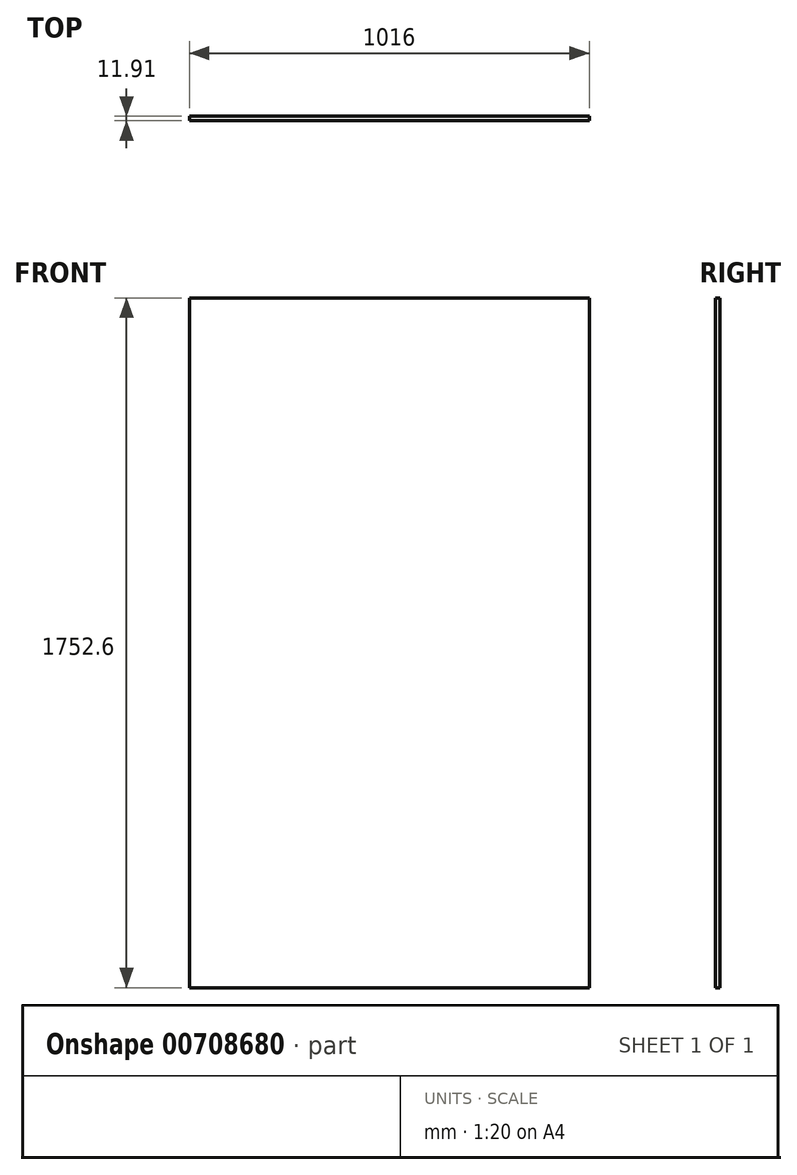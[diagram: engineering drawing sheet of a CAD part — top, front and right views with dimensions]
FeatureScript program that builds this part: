
annotation { "Feature Type Name" : "Feature", "Feature Type Description" : "" }
export const myFeature = defineFeature(function(context is Context, id is Id, definition is map)
    precondition{}
    {
        {
            var Q0;
            Q0=qCreatedBy(makeId("Front.planeOp"),FACE);
            var sketch = newSketch(context, id + "F0", { "sketchPlane" : qUnion([Q0])});
            skLineSegment(sketch, "E0.bottom", {"start": v(508, 876.3) * mm, "end": v(-508, 876.3) * mm});
            skLineSegment(sketch, "E0.top", {"start": v(508, -876.3) * mm, "end": v(-508, -876.3) * mm});
            skLineSegment(sketch, "E0.left", {"start": v(508, 876.3) * mm, "end": v(508, -876.3) * mm});
            skLineSegment(sketch, "E0.right", {"start": v(-508, 876.3) * mm, "end": v(-508, -876.3) * mm});
            skPoint(sketch, "E0.middle", {"position": v(0, 0) * mm});
            skSolve(sketch);
        }
        {
            var Q0;
            Q0=makeQuery(id+"F0.imprint","IMPRINT",FACE,{"disambiguationData":[TD([[makeQuery(id+"F0.imprint","IMPRINT",EDGE,{"derivedFrom":sQuery(id+"F0.wireOp",EDGE,"E0.bottom")}),1.0]])]});
            extrude(context, id + "F1", {"entities" : qUnion([Q0]), "depth" : 11.9 * mm, "offsetDistance" : 25.4 * mm});
        }
    });
